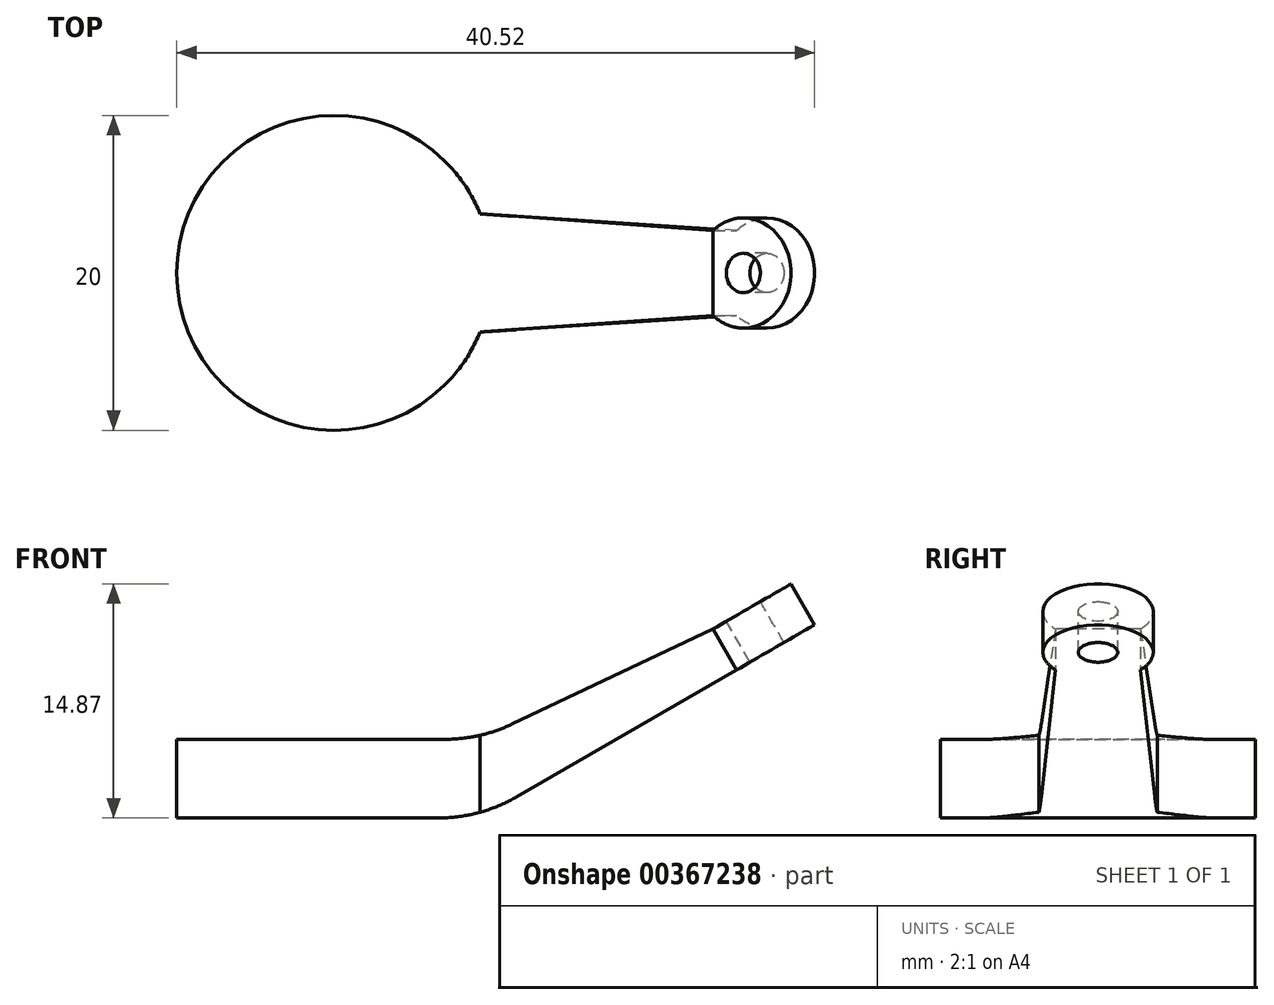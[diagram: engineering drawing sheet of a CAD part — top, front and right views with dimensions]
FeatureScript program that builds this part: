
annotation { "Feature Type Name" : "Feature", "Feature Type Description" : "" }
export const myFeature = defineFeature(function(context is Context, id is Id, definition is map)
    precondition{}
    {
        {
            var Q0;
            Q0=qCreatedBy(makeId("Top.planeOp"),FACE);
            var sketch = newSketch(context, id + "F0", { "sketchPlane" : qUnion([Q0])});
            skCircle(sketch, "E0", {"center": v(0, 0) * mm, "radius": 10 * mm});
            skLineSegment(sketch, "E1.bottom", {"start": v(9.27, 3.75) * mm, "end": v(10.73, 3.75) * mm});
            skLineSegment(sketch, "E1.top", {"start": v(9.27, -3.75) * mm, "end": v(10.73, -3.75) * mm});
            skLineSegment(sketch, "E1.left", {"start": v(9.27, 3.75) * mm, "end": v(9.27, -3.75) * mm});
            skLineSegment(sketch, "E1.right", {"start": v(10.73, 3.75) * mm, "end": v(10.73, -3.75) * mm});
            skSolve(sketch);
        }
        {
            var Q0;
            {var subQ0=sQuery(id+"F0.wireOp",EDGE,"E1.left");Q0=makeQuery(id+"F0.imprint","IMPRINT",FACE,{"disambiguationData":[TD([[makeQuery(id+"F0.imprint","IMPRINT",EDGE,{"derivedFrom":subQ0}),-1.0]])]});}
            extrude(context, id + "F1", {"entities" : qUnion([Q0]), "depth" : 5 * mm});
        }
        {
            var Q0;
            Q0=makeQuery(id+"F1.opExtrude","CAP_EDGE",EDGE,{"disambiguationData":[OSD([sQuery(id+"F0.wireOp",EDGE,"E1.left")])],"isStart":true});
            cPlane(context, id + "F2", {"entities" : qUnion([Q0]), "cplaneType" : CPlaneType.LINE_ANGLE, "offset" : 25 * mm, "angle" : 30 * degree, "width" : 150 * mm, "height" : 150 * mm});
        }
        {
            var Q0;
            Q0=qCreatedBy(id+"F2.planeOp",FACE);
            var sketch = newSketch(context, id + "F3", { "sketchPlane" : qUnion([Q0])});
            skCircle(sketch, "E2", {"center": v(29.06, 0) * mm, "radius": 3.5 * mm});
            skLineSegment(sketch, "E3.bottom", {"start": v(26.84, -2.7) * mm, "end": v(24.84, -2.7) * mm});
            skLineSegment(sketch, "E3.top", {"start": v(26.84, 2.7) * mm, "end": v(24.84, 2.7) * mm});
            skLineSegment(sketch, "E3.left", {"start": v(26.84, -2.7) * mm, "end": v(26.84, 2.7) * mm});
            skLineSegment(sketch, "E3.right", {"start": v(24.84, -2.7) * mm, "end": v(24.84, 2.7) * mm});
            skSolve(sketch);
        }
        {
            var Q0;
            {var subQ0=sQuery(id+"F3.wireOp",EDGE,"E3.left");Q0=makeQuery(id+"F3.imprint","IMPRINT",FACE,{"disambiguationData":[TD([[makeQuery(id+"F3.imprint","IMPRINT",EDGE,{"derivedFrom":subQ0}),-1.0]])]});}
            extrude(context, id + "F4", {"entities" : qUnion([Q0]), "oppositeDirection" : true, "depth" : 3 * mm});
        }
        {
            var Q0;
            Q0=makeQuery(id+"F4.opExtrude","SWEPT_FACE",FACE,{"disambiguationData":[OSD([sQuery(id+"F3.wireOp",EDGE,"E3.left")])]});
            var Q1;
            Q1=makeQuery(id+"F1.opExtrude","SWEPT_FACE",FACE,{"disambiguationData":[OSD([sQuery(id+"F0.wireOp",EDGE,"E1.left")])]});
            loft(context, id + "F5", {"operationType" : NewBodyOperationType.ADD, "sheetProfilesArray" : [{ "sheetProfileEntities" : qUnion([Q0]) }, { "sheetProfileEntities" : qUnion([Q1]) }]});
        }
        {
            var Q0;
            Q0=makeQuery(id+"F4.opExtrude","CAP_FACE",FACE,{"disambiguationData":[OSD([sQuery(id+"F3.wireOp",EDGE,"E2"),sQuery(id+"F3.wireOp",EDGE,"E3.left")])],"isStart":false});
            var sketch = newSketch(context, id + "F6", { "sketchPlane" : qUnion([Q0])});
            skCircle(sketch, "E4", {"center": v(29.06, 0) * mm, "radius": 1.25 * mm});
            skSolve(sketch);
        }
        {
            var Q0;
            Q0=makeQuery(id+"F6.imprint","IMPRINT",FACE,{"disambiguationData":[TD([[makeQuery(id+"F6.imprint","IMPRINT",EDGE,{"derivedFrom":sQuery(id+"F6.wireOp",EDGE,"E4")}),1.0]])]});
            extrude(context, id + "F7", {"entities" : qUnion([Q0]), "operationType" : NewBodyOperationType.REMOVE, "endBound" : BoundingType.THROUGH_ALL, "oppositeDirection" : true, "depth" : 25 * mm});
        }
        {
            var Q0;
            {var subQ0=sQuery(id+"F0.wireOp",EDGE,"E1.left");var subQ1=makeQuery(id+"F1.opExtrude","CAP_EDGE",EDGE,{"disambiguationData":[OSD([subQ0])],"isStart":false});var subQ2=sQuery(id+"F0.wireOp",EDGE,"E1.top");var subQ3=sQuery(id+"F0.wireOp",EDGE,"E0");var subQ4=sQuery(id+"F0.wireOp",EDGE,"E1.bottom");Q0=makeQuery(id+"F5.boolean.opBoolean","MERGE",EDGE,{"derivedFrom":[subQ1,makeQuery(id+"F5.opLoft","MID_CAP_EDGE",EDGE,{"disambiguationData":[OSD([subQ3,subQ4,subQ2,subQ0]),TDD([makeQuery(id+"F1.opExtrude","CAP_VERTEX",VERTEX,{"disambiguationData":[OSD([subQ3,subQ4,subQ0])],"isStart":false}),makeQuery(id+"F1.opExtrude","CAP_VERTEX",VERTEX,{"disambiguationData":[OSD([subQ3,subQ2,subQ0])],"isStart":false}),subQ1])],"capPos":1.0})]});}
            var Q1;
            {var subQ0=sQuery(id+"F0.wireOp",EDGE,"E1.left");var subQ1=makeQuery(id+"F1.opExtrude","CAP_EDGE",EDGE,{"disambiguationData":[OSD([subQ0])],"isStart":true});var subQ2=sQuery(id+"F0.wireOp",EDGE,"E1.top");var subQ3=sQuery(id+"F0.wireOp",EDGE,"E0");var subQ4=sQuery(id+"F0.wireOp",EDGE,"E1.bottom");Q1=makeQuery(id+"F5.boolean.opBoolean","MERGE",EDGE,{"derivedFrom":[subQ1,makeQuery(id+"F5.opLoft","MID_CAP_EDGE",EDGE,{"disambiguationData":[OSD([subQ3,subQ4,subQ2,subQ0]),TDD([makeQuery(id+"F1.opExtrude","CAP_VERTEX",VERTEX,{"disambiguationData":[OSD([subQ3,subQ4,subQ0])],"isStart":true}),makeQuery(id+"F1.opExtrude","CAP_VERTEX",VERTEX,{"disambiguationData":[OSD([subQ3,subQ2,subQ0])],"isStart":true}),subQ1])],"capPos":1.0})]});}
            fillet(context, id + "F8", {"entities" : qUnion([Q0, Q1]), "radius" : 10 * mm, "tangentPropagation" : true, "allowEdgeOverflow" : false});
        }
    });
